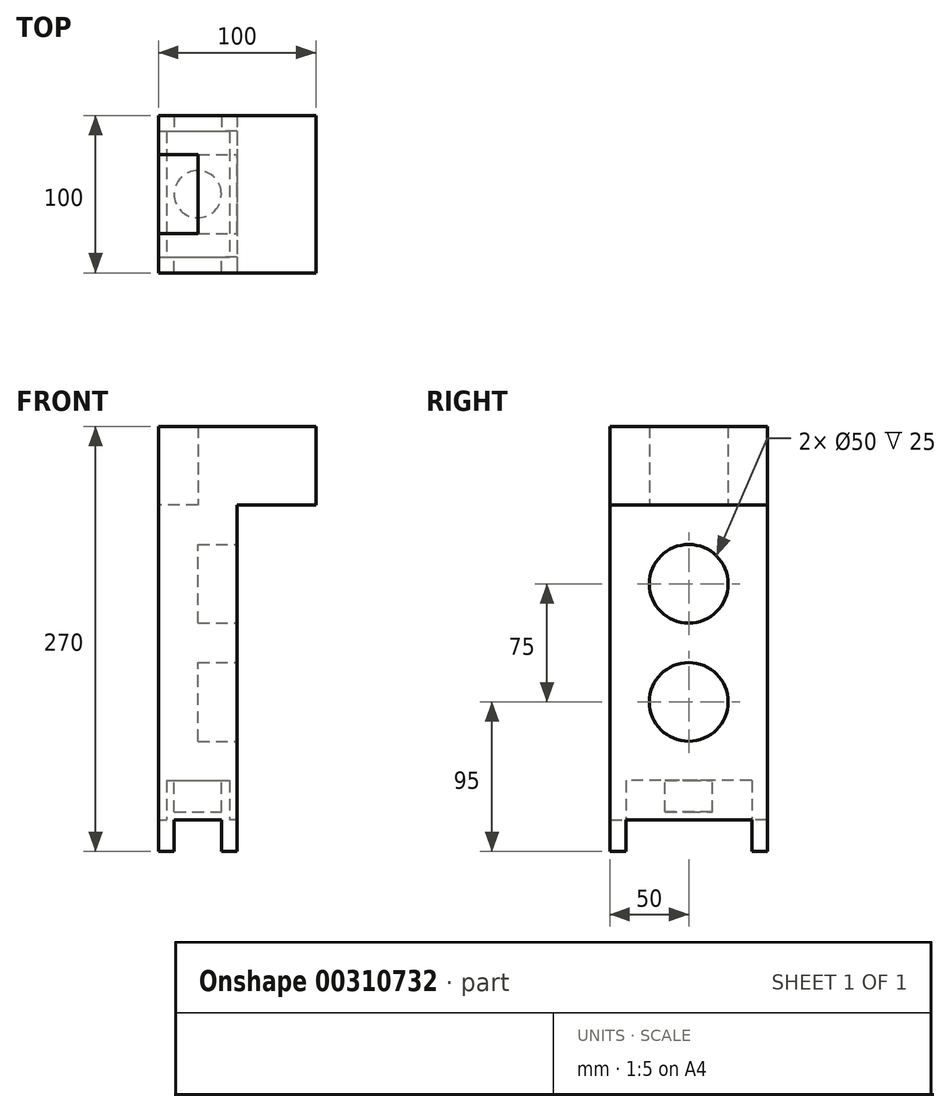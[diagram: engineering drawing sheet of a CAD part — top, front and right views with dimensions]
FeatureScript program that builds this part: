
annotation { "Feature Type Name" : "Feature", "Feature Type Description" : "" }
export const myFeature = defineFeature(function(context is Context, id is Id, definition is map)
    precondition{}
    {
        {
            var Q0;
            Q0=qCreatedBy(makeId("Front.planeOp"),FACE);
            var sketch = newSketch(context, id + "F0", { "sketchPlane" : qUnion([Q0])});
            skLineSegment(sketch, "E0.bottom", {"start": v(25, -100) * mm, "end": v(-25, -100) * mm});
            skLineSegment(sketch, "E0.left", {"start": v(25, -100) * mm, "end": v(25, 100) * mm});
            skLineSegment(sketch, "E0.right", {"start": v(-25, -100) * mm, "end": v(-25, 100) * mm});
            skPoint(sketch, "E0.middle", {"position": v(0, 0) * mm});
            skLineSegment(sketch, "E1", {"start": v(25, 100) * mm, "end": v(75, 100) * mm});
            skLineSegment(sketch, "E2", {"start": v(75, 150) * mm, "end": v(75, 100) * mm});
            skLineSegment(sketch, "E3", {"start": v(75, 150) * mm, "end": v(-25, 150) * mm});
            skLineSegment(sketch, "E4", {"start": v(-25, 100) * mm, "end": v(-25, 150) * mm});
            skSolve(sketch);
        }
        {
            var Q0;
            Q0=makeQuery(id+"F0.imprint","IMPRINT",FACE,{"disambiguationData":[TD([[makeQuery(id+"F0.imprint","IMPRINT",EDGE,{"derivedFrom":sQuery(id+"F0.wireOp",EDGE,"E0.bottom")}),-1.0]])]});
            extrude(context, id + "F1", {"entities" : qUnion([Q0]), "oppositeDirection" : true, "depth" : 100 * mm});
        }
        {
            var Q0;
            Q0=makeQuery(id+"F1.opExtrude","SWEPT_FACE",FACE,{"disambiguationData":[OSD([sQuery(id+"F0.wireOp",EDGE,"E0.left")])]});
            var sketch = newSketch(context, id + "F2", { "sketchPlane" : qUnion([Q0])});
            skCircle(sketch, "E5", {"center": v(50, 50) * mm, "radius": 25 * mm});
            skCircle(sketch, "E6", {"center": v(50, -25) * mm, "radius": 25 * mm});
            skSolve(sketch);
        }
        {
            var Q0;
            Q0=makeQuery(id+"F2.imprint","IMPRINT",FACE,{"disambiguationData":[TD([[makeQuery(id+"F2.imprint","IMPRINT",EDGE,{"derivedFrom":sQuery(id+"F2.wireOp",EDGE,"E6")}),1.0]])]});
            var Q1;
            Q1=makeQuery(id+"F2.imprint","IMPRINT",FACE,{"disambiguationData":[TD([[makeQuery(id+"F2.imprint","IMPRINT",EDGE,{"derivedFrom":sQuery(id+"F2.wireOp",EDGE,"E5")}),1.0]])]});
            extrude(context, id + "F3", {"entities" : qUnion([Q0, Q1]), "operationType" : NewBodyOperationType.REMOVE, "oppositeDirection" : true, "depth" : 25 * mm});
        }
        {
            var Q0;
            Q0=makeQuery(id+"F1.opExtrude","SWEPT_FACE",FACE,{"disambiguationData":[OSD([sQuery(id+"F0.wireOp",EDGE,"E3")])]});
            var sketch = newSketch(context, id + "F4", { "sketchPlane" : qUnion([Q0])});
            skCircle(sketch, "E7", {"center": v(23.97, 50) * mm, "radius": 15 * mm});
            skPoint(sketch, "E7.centerSnap0", {"position": v(75, 50) * mm});
            skSolve(sketch);
        }
        {
            var Q0;
            Q0=makeQuery(id+"F1.opExtrude","SWEPT_FACE",FACE,{"disambiguationData":[OSD([sQuery(id+"F0.wireOp",EDGE,"E0.bottom")])]});
            var sketch = newSketch(context, id + "F5", { "sketchPlane" : qUnion([Q0])});
            skPoint(sketch, "E8.endSnap0", {"position": v(0, 0) * mm});
            skLineSegment(sketch, "E9.bottom", {"start": v(-20, -90) * mm, "end": v(20, -90) * mm});
            skLineSegment(sketch, "E9.top", {"start": v(-20, -10) * mm, "end": v(20, -10) * mm});
            skLineSegment(sketch, "E9.left", {"start": v(-20, -90) * mm, "end": v(-20, -10) * mm});
            skLineSegment(sketch, "E9.right", {"start": v(20, -90) * mm, "end": v(20, -10) * mm});
            skPoint(sketch, "E9.middle", {"position": v(0, -50) * mm});
            skSolve(sketch);
        }
        {
            var Q0;
            Q0=makeQuery(id+"F5.imprint","IMPRINT",FACE,{"disambiguationData":[TD([[makeQuery(id+"F5.imprint","IMPRINT",EDGE,{"derivedFrom":sQuery(id+"F5.wireOp",EDGE,"E9.bottom")}),1.0]])]});
            extrude(context, id + "F6", {"entities" : qUnion([Q0]), "operationType" : NewBodyOperationType.REMOVE, "oppositeDirection" : true, "depth" : 25 * mm});
        }
        {
            var Q0;
            Q0=makeQuery(id+"F6.boolean.opBoolean","COPY",FACE,{"derivedFrom":makeQuery(id+"F6.opExtrude","CAP_FACE",FACE,{"disambiguationData":[OSD([sQuery(id+"F5.wireOp",EDGE,"E9.bottom"),sQuery(id+"F5.wireOp",EDGE,"E9.top"),sQuery(id+"F5.wireOp",EDGE,"E9.left"),sQuery(id+"F5.wireOp",EDGE,"E9.right")])],"isStart":false})});
            var sketch = newSketch(context, id + "F7", { "sketchPlane" : qUnion([Q0])});
            skLineSegment(sketch, "E10", {"start": v(20, -50) * mm, "end": v(0, -50) * mm});
            skCircle(sketch, "E11", {"center": v(0, -50) * mm, "radius": 15 * mm});
            skSolve(sketch);
        }
        {
            var Q0;
            Q0=makeQuery(id+"F7.imprint","IMPRINT",FACE,{"disambiguationData":[TD([[makeQuery(id+"F7.imprint","IMPRINT",EDGE,{"derivedFrom":sQuery(id+"F7.wireOp",EDGE,"E11")}),1.0]])]});
            extrude(context, id + "F8", {"entities" : qUnion([Q0]), "operationType" : NewBodyOperationType.ADD, "depth" : 20 * mm});
        }
        {
            var Q0;
            Q0=makeQuery(id+"F1.opExtrude","SWEPT_FACE",FACE,{"disambiguationData":[OSD([sQuery(id+"F0.wireOp",EDGE,"E0.bottom")])]});
            var sketch = newSketch(context, id + "F9", { "sketchPlane" : qUnion([Q0])});
            skLineSegment(sketch, "E12.bottom", {"start": v(25, -100) * mm, "end": v(15, -100) * mm});
            skLineSegment(sketch, "E12.top", {"start": v(25, -90) * mm, "end": v(15, -90) * mm});
            skLineSegment(sketch, "E12.left", {"start": v(25, -100) * mm, "end": v(25, -90) * mm});
            skLineSegment(sketch, "E12.right", {"start": v(15, -100) * mm, "end": v(15, -90) * mm});
            skLineSegment(sketch, "E13.bottom", {"start": v(25, 0) * mm, "end": v(15, 0) * mm});
            skLineSegment(sketch, "E13.top", {"start": v(25, -10) * mm, "end": v(15, -10) * mm});
            skLineSegment(sketch, "E13.left", {"start": v(25, 0) * mm, "end": v(25, -10) * mm});
            skLineSegment(sketch, "E13.right", {"start": v(15, 0) * mm, "end": v(15, -10) * mm});
            skLineSegment(sketch, "E14.bottom", {"start": v(-25, 0) * mm, "end": v(-15, 0) * mm});
            skLineSegment(sketch, "E14.top", {"start": v(-25, -10) * mm, "end": v(-15, -10) * mm});
            skLineSegment(sketch, "E14.left", {"start": v(-25, 0) * mm, "end": v(-25, -10) * mm});
            skLineSegment(sketch, "E14.right", {"start": v(-15, 0) * mm, "end": v(-15, -10) * mm});
            skLineSegment(sketch, "E15.bottom", {"start": v(-25, -100) * mm, "end": v(-15, -100) * mm});
            skLineSegment(sketch, "E15.top", {"start": v(-25, -90) * mm, "end": v(-15, -90) * mm});
            skLineSegment(sketch, "E15.left", {"start": v(-25, -100) * mm, "end": v(-25, -90) * mm});
            skLineSegment(sketch, "E15.right", {"start": v(-15, -100) * mm, "end": v(-15, -90) * mm});
            skSolve(sketch);
        }
        {
            var Q0;
            Q0=makeQuery(id+"F9.imprint","IMPRINT",FACE,{"disambiguationData":[TD([[makeQuery(id+"F9.imprint","IMPRINT",EDGE,{"derivedFrom":sQuery(id+"F9.wireOp",EDGE,"E14.bottom")}),1.0]])]});
            var Q1;
            Q1=makeQuery(id+"F9.imprint","IMPRINT",FACE,{"disambiguationData":[TD([[makeQuery(id+"F9.imprint","IMPRINT",EDGE,{"derivedFrom":sQuery(id+"F9.wireOp",EDGE,"E13.bottom")}),1.0]])]});
            var Q2;
            Q2=makeQuery(id+"F9.imprint","IMPRINT",FACE,{"disambiguationData":[TD([[makeQuery(id+"F9.imprint","IMPRINT",EDGE,{"derivedFrom":sQuery(id+"F9.wireOp",EDGE,"E12.bottom")}),-1.0]])]});
            var Q3;
            Q3=makeQuery(id+"F9.imprint","IMPRINT",FACE,{"disambiguationData":[TD([[makeQuery(id+"F9.imprint","IMPRINT",EDGE,{"derivedFrom":sQuery(id+"F9.wireOp",EDGE,"E15.bottom")}),-1.0]])]});
            extrude(context, id + "F10", {"entities" : qUnion([Q0, Q1, Q2, Q3]), "operationType" : NewBodyOperationType.ADD, "depth" : 20 * mm});
        }
        {
            var Q0;
            Q0=makeQuery(id+"F10.boolean.opBoolean","MERGE",FACE,{"derivedFrom":[makeQuery(id+"F1.opExtrude","SWEPT_FACE",FACE,{"disambiguationData":[OSD([sQuery(id+"F0.wireOp",EDGE,"E0.right"),sQuery(id+"F0.wireOp",EDGE,"E4")])]}),makeQuery(id+"F10.opExtrude","SWEPT_FACE",FACE,{"disambiguationData":[OSD([sQuery(id+"F9.wireOp",EDGE,"E14.left")])]}),makeQuery(id+"F10.opExtrude","SWEPT_FACE",FACE,{"disambiguationData":[OSD([sQuery(id+"F9.wireOp",EDGE,"E15.left")])]})]});
            var sketch = newSketch(context, id + "F11", { "sketchPlane" : qUnion([Q0])});
            skLineSegment(sketch, "E16.top", {"start": v(-75, 100) * mm, "end": v(-25, 100) * mm});
            skLineSegment(sketch, "E16.left", {"start": v(-75, 150) * mm, "end": v(-75, 100) * mm});
            skLineSegment(sketch, "E16.right", {"start": v(-25, 150) * mm, "end": v(-25, 100) * mm});
            skSolve(sketch);
        }
        {
            var Q0;
            Q0=makeQuery(id+"F11.imprint","IMPRINT",FACE,{"disambiguationData":[TD([[makeQuery(id+"F11.imprint","IMPRINT",EDGE,{"derivedFrom":sQuery(id+"F11.wireOp",EDGE,"E16.top")}),1.0]])]});
            extrude(context, id + "F12", {"entities" : qUnion([Q0]), "operationType" : NewBodyOperationType.REMOVE, "oppositeDirection" : true, "depth" : 25 * mm});
        }
    });
